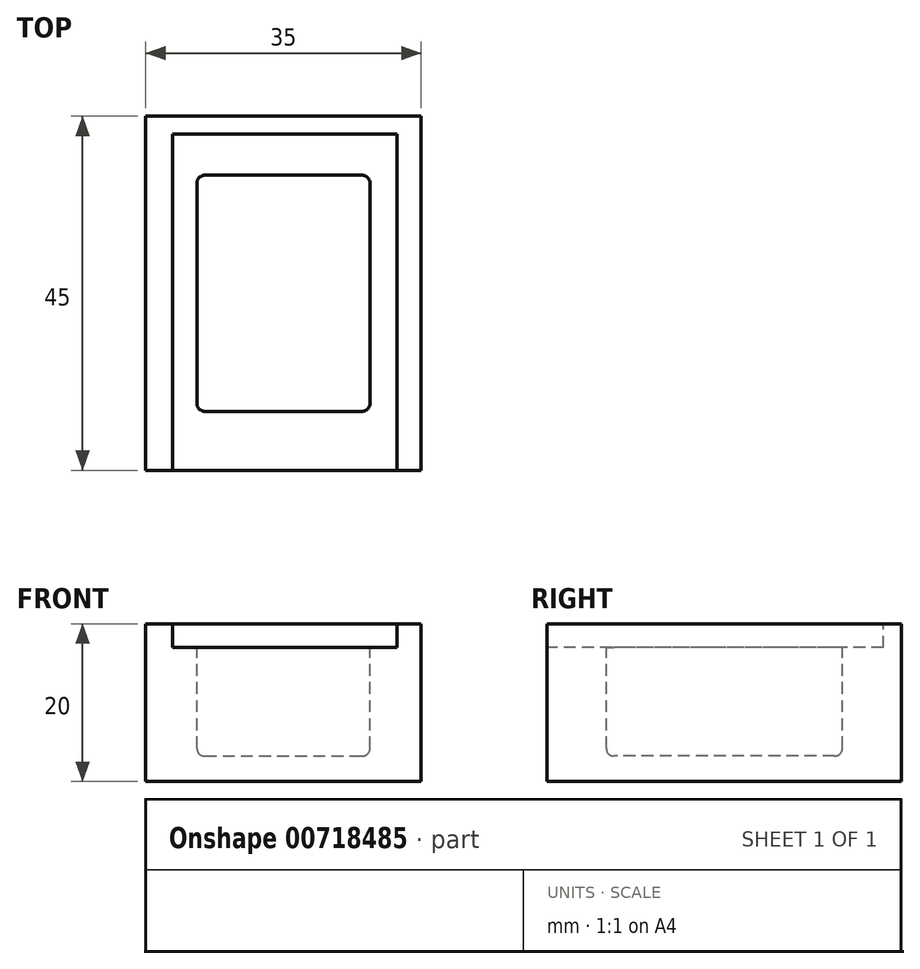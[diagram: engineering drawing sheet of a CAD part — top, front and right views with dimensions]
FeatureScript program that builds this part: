
annotation { "Feature Type Name" : "Feature", "Feature Type Description" : "" }
export const myFeature = defineFeature(function(context is Context, id is Id, definition is map)
    precondition{}
    {
        {
            var Q0;
            Q0=qCreatedBy(makeId("Top.planeOp"),FACE);
            var sketch = newSketch(context, id + "F0", { "sketchPlane" : qUnion([Q0])});
            skLineSegment(sketch, "E0.bottom", {"start": v(-17.5, 22.5) * mm, "end": v(17.5, 22.5) * mm});
            skLineSegment(sketch, "E0.top", {"start": v(-17.5, -22.5) * mm, "end": v(17.5, -22.5) * mm});
            skLineSegment(sketch, "E0.left", {"start": v(-17.5, 22.5) * mm, "end": v(-17.5, -22.5) * mm});
            skLineSegment(sketch, "E0.right", {"start": v(17.5, 22.5) * mm, "end": v(17.5, -22.5) * mm});
            skLineSegment(sketch, "E1", {"start": v(0, 20.07) * mm, "end": v(0, 0) * mm});
            skLineSegment(sketch, "E2", {"start": v(0, 0) * mm, "end": v(0, 20.07) * mm});
            skLineSegment(sketch, "E3", {"start": v(0, 22.5) * mm, "end": v(0, 20.07) * mm});
            skLineSegment(sketch, "E4", {"start": v(-14.6, 0) * mm, "end": v(-17.5, 0) * mm});
            skPoint(sketch, "E4.endSnap0", {"position": v(-17.5, 0) * mm});
            skLineSegment(sketch, "E5", {"start": v(0, 0) * mm, "end": v(-14.6, 0) * mm});
            skPoint(sketch, "E6.orphan", {"position": v(-14.6, 20.07) * mm});
            skPoint(sketch, "E7.right.start.orphan", {"position": v(14.6, 20.07) * mm});
            skPoint(sketch, "E7.left.end.orphan", {"position": v(-14.6, -20.07) * mm});
            skSolve(sketch);
        }
        {
            var Q0;
            Q0 = qSketchRegion(id + "F0", true);
            extrude(context, id + "F1", {"entities" : qUnion([Q0]), "depth" : 20 * mm, "offsetDistance" : 25.4 * mm});
        }
        {
            var Q0;
            Q0=makeQuery(id+"F1.opExtrude","CAP_FACE",FACE,{"disambiguationData":[OSD([sQuery(id+"F0.wireOp",EDGE,"E0.bottom"),sQuery(id+"F0.wireOp",EDGE,"E0.top"),sQuery(id+"F0.wireOp",EDGE,"E0.left"),sQuery(id+"F0.wireOp",EDGE,"E0.right")])],"isStart":false});
            var sketch = newSketch(context, id + "F2", { "sketchPlane" : qUnion([Q0])});
            skLineSegment(sketch, "E8.bottom", {"start": v(-14.1, 20.21) * mm, "end": v(14.4, 20.21) * mm});
            skLineSegment(sketch, "E8.top", {"start": v(-14.1, -20.29) * mm, "end": v(14.4, -20.29) * mm});
            skLineSegment(sketch, "E8.left", {"start": v(-14.1, 20.21) * mm, "end": v(-14.1, -20.29) * mm});
            skLineSegment(sketch, "E8.right", {"start": v(14.4, 20.21) * mm, "end": v(14.4, -20.29) * mm});
            skLineSegment(sketch, "E9", {"start": v(0.16, 20.21) * mm, "end": v(0.16, 22.5) * mm});
            skLineSegment(sketch, "E10", {"start": v(-14.1, 0) * mm, "end": v(-17.5, 0) * mm});
            skSolve(sketch);
        }
        {
            var Q0;
            {var subQ4=sQuery(id+"F2.wireOp",EDGE,"E8.top");Q0=makeQuery(id+"F2.imprint","IMPRINT",FACE,{"disambiguationData":[TD([[makeQuery(id+"F2.imprint","IMPRINT",EDGE,{"derivedFrom":subQ4}),1.0]])]});}
            extrude(context, id + "F3", {"entities" : qUnion([Q0]), "operationType" : NewBodyOperationType.REMOVE, "oppositeDirection" : true, "depth" : 3 * mm, "offsetDistance" : 25.4 * mm});
        }
        {
            var Q0;
            Q0=makeQuery(id+"F3.boolean.opBoolean","COPY",FACE,{"derivedFrom":makeQuery(id+"F3.opExtrude","CAP_FACE",FACE,{"disambiguationData":[OSD([sQuery(id+"F2.wireOp",EDGE,"E8.bottom"),sQuery(id+"F2.wireOp",EDGE,"E8.top"),sQuery(id+"F2.wireOp",EDGE,"E8.left"),sQuery(id+"F2.wireOp",EDGE,"E8.right")])],"isStart":false})});
            var sketch = newSketch(context, id + "F4", { "sketchPlane" : qUnion([Q0])});
            skLineSegment(sketch, "E11.bottom", {"start": v(-11, 15) * mm, "end": v(11, 15) * mm});
            skLineSegment(sketch, "E11.top", {"start": v(-11, -15) * mm, "end": v(11, -15) * mm});
            skLineSegment(sketch, "E11.left", {"start": v(-11, 15) * mm, "end": v(-11, -15) * mm});
            skLineSegment(sketch, "E11.right", {"start": v(11, 15) * mm, "end": v(11, -15) * mm});
            skPoint(sketch, "E11.middle", {"position": v(0, 0) * mm});
            skSolve(sketch);
        }
        {
            var Q0;
            Q0=makeQuery(id+"F4.imprint","IMPRINT",FACE,{"disambiguationData":[TD([[makeQuery(id+"F4.imprint","IMPRINT",EDGE,{"derivedFrom":sQuery(id+"F4.wireOp",EDGE,"E11.bottom")}),-1.0]])]});
            extrude(context, id + "F5", {"entities" : qUnion([Q0]), "operationType" : NewBodyOperationType.REMOVE, "oppositeDirection" : true, "depth" : 13.8 * mm, "offsetDistance" : 25.4 * mm});
        }
        {
            var Q0;
            Q0=makeQuery(id+"F1.opExtrude","CAP_FACE",FACE,{"disambiguationData":[OSD([sQuery(id+"F0.wireOp",EDGE,"E0.bottom"),sQuery(id+"F0.wireOp",EDGE,"E0.top"),sQuery(id+"F0.wireOp",EDGE,"E0.left"),sQuery(id+"F0.wireOp",EDGE,"E0.right")])],"isStart":false});
            var sketch = newSketch(context, id + "F6", { "sketchPlane" : qUnion([Q0])});
            skLineSegment(sketch, "E12.bottom", {"start": v(-14.1, -20.29) * mm, "end": v(14.4, -20.29) * mm});
            skLineSegment(sketch, "E12.top", {"start": v(-14.1, -22.5) * mm, "end": v(14.4, -22.5) * mm});
            skLineSegment(sketch, "E12.left", {"start": v(-14.1, -20.29) * mm, "end": v(-14.1, -22.5) * mm});
            skLineSegment(sketch, "E12.right", {"start": v(14.4, -20.29) * mm, "end": v(14.4, -22.5) * mm});
            skSolve(sketch);
        }
        {
            var Q0;
            Q0 = qSketchRegion(id + "F6", true);
            var Q1;
            Q1=makeQuery(id+"F3.boolean.opBoolean","COPY",FACE,{"derivedFrom":makeQuery(id+"F3.opExtrude","CAP_FACE",FACE,{"disambiguationData":[OSD([sQuery(id+"F2.wireOp",EDGE,"E8.bottom"),sQuery(id+"F2.wireOp",EDGE,"E8.top"),sQuery(id+"F2.wireOp",EDGE,"E8.left"),sQuery(id+"F2.wireOp",EDGE,"E8.right")])],"isStart":false})});
            extrude(context, id + "F7", {"entities" : qUnion([Q0]), "operationType" : NewBodyOperationType.REMOVE, "endBound" : BoundingType.UP_TO_SURFACE, "oppositeDirection" : true, "depth" : 25.4 * mm, "endBoundEntityFace" : qUnion([Q1]), "offsetDistance" : 25.4 * mm});
        }
        {
            var Q0;
            Q0=makeQuery(id+"F5.boolean.opBoolean","COPY",EDGE,{"derivedFrom":makeQuery(id+"F5.opExtrude","CAP_EDGE",EDGE,{"disambiguationData":[OSD([sQuery(id+"F4.wireOp",EDGE,"E11.left")])],"isStart":false})});
            var Q1;
            Q1=makeQuery(id+"F5.boolean.opBoolean","COPY",EDGE,{"derivedFrom":makeQuery(id+"F5.opExtrude","CAP_EDGE",EDGE,{"disambiguationData":[OSD([sQuery(id+"F4.wireOp",EDGE,"E11.top")])],"isStart":false})});
            var Q2;
            Q2=makeQuery(id+"F5.boolean.opBoolean","COPY",EDGE,{"derivedFrom":makeQuery(id+"F5.opExtrude","CAP_EDGE",EDGE,{"disambiguationData":[OSD([sQuery(id+"F4.wireOp",EDGE,"E11.bottom")])],"isStart":false})});
            var Q3;
            Q3=makeQuery(id+"F5.boolean.opBoolean","COPY",EDGE,{"derivedFrom":makeQuery(id+"F5.opExtrude","CAP_EDGE",EDGE,{"disambiguationData":[OSD([sQuery(id+"F4.wireOp",EDGE,"E11.right")])],"isStart":false})});
            var Q4;
            Q4=makeQuery(id+"F5.boolean.opBoolean","COPY",EDGE,{"derivedFrom":makeQuery(id+"F5.opExtrude","CAP_EDGE",EDGE,{"disambiguationData":[OSD([sQuery(id+"F4.wireOp",EDGE,"E11.bottom")])],"isStart":true})});
            var Q5;
            Q5=makeQuery(id+"F5.boolean.opBoolean","COPY",EDGE,{"derivedFrom":makeQuery(id+"F5.opExtrude","CAP_EDGE",EDGE,{"disambiguationData":[OSD([sQuery(id+"F4.wireOp",EDGE,"E11.right")])],"isStart":true})});
            var Q6;
            Q6=makeQuery(id+"F5.boolean.opBoolean","COPY",EDGE,{"derivedFrom":makeQuery(id+"F5.opExtrude","CAP_EDGE",EDGE,{"disambiguationData":[OSD([sQuery(id+"F4.wireOp",EDGE,"E11.left")])],"isStart":true})});
            var Q7;
            Q7=makeQuery(id+"F5.boolean.opBoolean","COPY",EDGE,{"derivedFrom":makeQuery(id+"F5.opExtrude","CAP_EDGE",EDGE,{"disambiguationData":[OSD([sQuery(id+"F4.wireOp",EDGE,"E11.top")])],"isStart":true})});
            var Q8;
            Q8=makeQuery(id+"F5.boolean.opBoolean","COPY",EDGE,{"derivedFrom":makeQuery(id+"F5.opExtrude","SWEPT_EDGE",EDGE,{"disambiguationData":[OSD([sQuery(id+"F4.wireOp",EDGE,"E11.bottom"),sQuery(id+"F4.wireOp",EDGE,"E11.right")])]})});
            var Q9;
            Q9=makeQuery(id+"F5.boolean.opBoolean","COPY",EDGE,{"derivedFrom":makeQuery(id+"F5.opExtrude","SWEPT_EDGE",EDGE,{"disambiguationData":[OSD([sQuery(id+"F4.wireOp",EDGE,"E11.bottom"),sQuery(id+"F4.wireOp",EDGE,"E11.left")])]})});
            var Q10;
            Q10=makeQuery(id+"F5.boolean.opBoolean","COPY",EDGE,{"derivedFrom":makeQuery(id+"F5.opExtrude","SWEPT_EDGE",EDGE,{"disambiguationData":[OSD([sQuery(id+"F4.wireOp",EDGE,"E11.top"),sQuery(id+"F4.wireOp",EDGE,"E11.right")])]})});
            var Q11;
            Q11=makeQuery(id+"F5.boolean.opBoolean","COPY",EDGE,{"derivedFrom":makeQuery(id+"F5.opExtrude","SWEPT_EDGE",EDGE,{"disambiguationData":[OSD([sQuery(id+"F4.wireOp",EDGE,"E11.top"),sQuery(id+"F4.wireOp",EDGE,"E11.left")])]})});
            fillet(context, id + "F8", {"entities" : qUnion([Q0, Q1, Q2, Q3, Q4, Q5, Q6, Q7, Q8, Q9, Q10, Q11]), "radius" : 1 * mm, "tangentPropagation" : true, "allowEdgeOverflow" : false});
        }
    });
